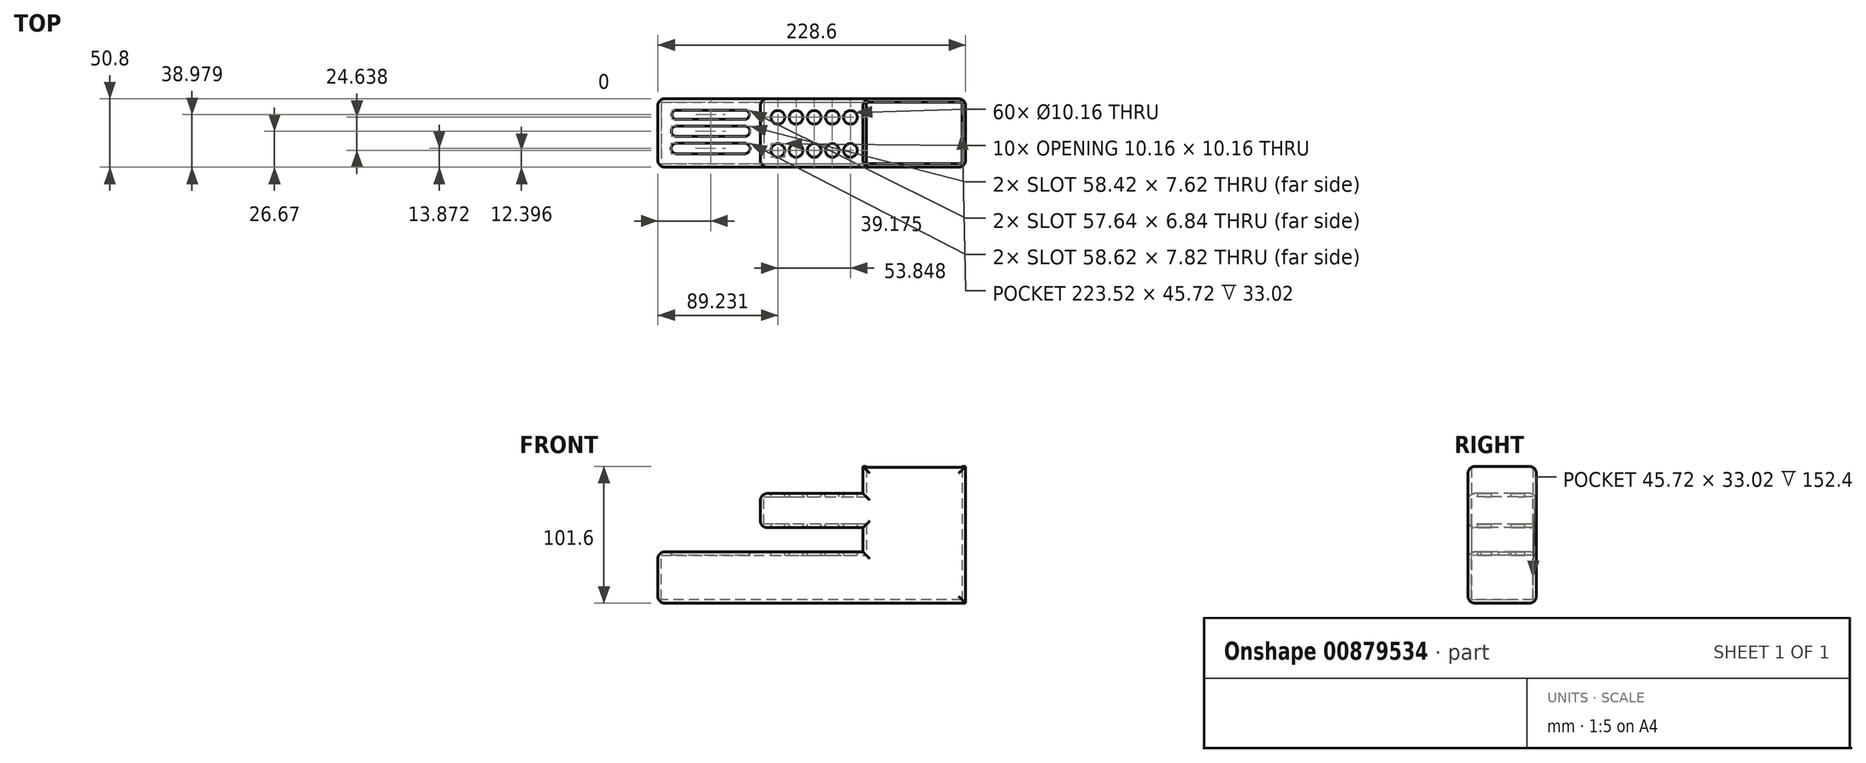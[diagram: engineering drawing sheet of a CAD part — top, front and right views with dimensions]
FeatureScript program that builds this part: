
annotation { "Feature Type Name" : "Feature", "Feature Type Description" : "" }
export const myFeature = defineFeature(function(context is Context, id is Id, definition is map)
    precondition{}
    {
        {
            var Q0;
            Q0=qCreatedBy(makeId("Front.planeOp"),FACE);
            var sketch = newSketch(context, id + "F0", { "sketchPlane" : qUnion([Q0])});
            skLineSegment(sketch, "E0", {"start": v(0, 45.54) * mm, "end": v(0, -56.06) * mm});
            skLineSegment(sketch, "E1", {"start": v(0, -56.06) * mm, "end": v(76.2, -56.06) * mm});
            skLineSegment(sketch, "E2", {"start": v(0, 45.54) * mm, "end": v(76.2, 45.54) * mm});
            skLineSegment(sketch, "E3", {"start": v(76.2, 45.54) * mm, "end": v(76.2, -56.06) * mm});
            skLineSegment(sketch, "E4", {"start": v(0, -56.06) * mm, "end": v(-152.4, -56.06) * mm});
            skLineSegment(sketch, "E5", {"start": v(-152.4, -56.06) * mm, "end": v(-152.4, -17.96) * mm});
            skLineSegment(sketch, "E6", {"start": v(-152.4, -17.96) * mm, "end": v(0, -17.96) * mm});
            skLineSegment(sketch, "E7", {"start": v(0, 0) * mm, "end": v(-76.2, 0) * mm});
            skLineSegment(sketch, "E8", {"start": v(-76.2, 0) * mm, "end": v(-76.2, 25.4) * mm});
            skLineSegment(sketch, "E9", {"start": v(-76.2, 25.4) * mm, "end": v(0, 25.4) * mm});
            skSolve(sketch);
        }
        {
            var Q0;
            Q0 = qSketchRegion(id + "F0", true);
            extrude(context, id + "F1", {"entities" : qUnion([Q0]), "oppositeDirection" : true, "depth" : 50.8 * mm, "offsetDistance" : 25.4 * mm});
        }
        {
            var Q0;
            Q0=makeQuery(id+"F1.opExtrude","SWEPT_FACE",FACE,{"disambiguationData":[OSD([sQuery(id+"F0.wireOp",EDGE,"E2")])]});
            shell(context, id + "F2", {"entities" : qUnion([Q0]), "thickness" : 2.54 * mm});
        }
        {
            var Q0;
            Q0=makeQuery(id+"F1.opExtrude","SWEPT_FACE",FACE,{"disambiguationData":[OSD([sQuery(id+"F0.wireOp",EDGE,"E9")])]});
            var sketch = newSketch(context, id + "F3", { "sketchPlane" : qUnion([Q0])});
            skCircle(sketch, "E10", {"center": v(-9.32, 12.4) * mm, "radius": 5.08 * mm});
            skCircle(sketch, "E11.0.1.0", {"center": v(-9.32, 37.03) * mm, "radius": 5.08 * mm});
            skCircle(sketch, "E11.1.0.0", {"center": v(-22.78, 12.4) * mm, "radius": 5.08 * mm});
            skCircle(sketch, "E11.1.1.0", {"center": v(-22.78, 37.03) * mm, "radius": 5.08 * mm});
            skCircle(sketch, "E11.2.0.0", {"center": v(-36.25, 12.4) * mm, "radius": 5.08 * mm});
            skCircle(sketch, "E11.2.1.0", {"center": v(-36.25, 37.03) * mm, "radius": 5.08 * mm});
            skCircle(sketch, "E11.3.0.0", {"center": v(-49.7, 12.4) * mm, "radius": 5.08 * mm});
            skCircle(sketch, "E11.3.1.0", {"center": v(-49.7, 37.03) * mm, "radius": 5.08 * mm});
            skCircle(sketch, "E11.4.0.0", {"center": v(-63.17, 12.4) * mm, "radius": 5.08 * mm});
            skCircle(sketch, "E11.4.1.0", {"center": v(-63.17, 37.03) * mm, "radius": 5.08 * mm});
            skLineSegment(sketch, "E11.direction1", {"start": v(-9.32, 12.4) * mm, "end": v(-22.78, 12.4) * mm, "construction": true});
            skLineSegment(sketch, "E11.direction2", {"start": v(-9.32, 12.4) * mm, "end": v(-9.32, 37.03) * mm, "construction": true});
            skSolve(sketch);
        }
        {
            var Q0;
            Q0 = qSketchRegion(id + "F3", true);
            extrude(context, id + "F4", {"entities" : qUnion([Q0]), "operationType" : NewBodyOperationType.REMOVE, "oppositeDirection" : true, "depth" : 76.2 * mm, "offsetDistance" : 25.4 * mm});
        }
        {
            var Q0;
            Q0=makeQuery(id+"F1.opExtrude","CAP_FACE",FACE,{"disambiguationData":[OSD([sQuery(id+"F0.wireOp",EDGE,"E0"),sQuery(id+"F0.wireOp",EDGE,"E1"),sQuery(id+"F0.wireOp",EDGE,"E2"),sQuery(id+"F0.wireOp",EDGE,"E3"),sQuery(id+"F0.wireOp",EDGE,"E4"),sQuery(id+"F0.wireOp",EDGE,"E5"),sQuery(id+"F0.wireOp",EDGE,"E6"),sQuery(id+"F0.wireOp",EDGE,"E7"),sQuery(id+"F0.wireOp",EDGE,"E8"),sQuery(id+"F0.wireOp",EDGE,"E9")])],"isStart":true});
            var Q1;
            Q1=makeQuery(id+"F1.opExtrude","CAP_FACE",FACE,{"disambiguationData":[OSD([sQuery(id+"F0.wireOp",EDGE,"E0"),sQuery(id+"F0.wireOp",EDGE,"E1"),sQuery(id+"F0.wireOp",EDGE,"E2"),sQuery(id+"F0.wireOp",EDGE,"E3"),sQuery(id+"F0.wireOp",EDGE,"E4"),sQuery(id+"F0.wireOp",EDGE,"E5"),sQuery(id+"F0.wireOp",EDGE,"E6"),sQuery(id+"F0.wireOp",EDGE,"E7"),sQuery(id+"F0.wireOp",EDGE,"E8"),sQuery(id+"F0.wireOp",EDGE,"E9")])],"isStart":false});
            var Q2;
            Q2=makeQuery(id+"F1.opExtrude","SWEPT_FACE",FACE,{"disambiguationData":[OSD([sQuery(id+"F0.wireOp",EDGE,"E5")])]});
            var Q3;
            Q3=makeQuery(id+"F1.opExtrude","SWEPT_FACE",FACE,{"disambiguationData":[OSD([sQuery(id+"F0.wireOp",EDGE,"E8")])]});
            fillet(context, id + "F5", {"entities" : qUnion([Q0, Q1, Q2, Q3]), "radius" : 5.08 * mm, "tangentPropagation" : true, "allowEdgeOverflow" : false});
        }
        {
            var Q0;
            Q0=makeQuery(id+"F1.opExtrude","SWEPT_FACE",FACE,{"disambiguationData":[OSD([sQuery(id+"F0.wireOp",EDGE,"E6")])]});
            var sketch = newSketch(context, id + "F6", { "sketchPlane" : qUnion([Q0])});
            skLineSegment(sketch, "E12", {"start": v(-138.63, 9.96) * mm, "end": v(-87.83, 9.96) * mm});
            skLineSegment(sketch, "E13", {"start": v(-138.63, 17.78) * mm, "end": v(-87.83, 17.78) * mm});
            skArc(sketch, "E14", {"start": v(-138.63, 9.96) * mm, "mid": v(-142.53, 13.87) * mm, "end": v(-138.63, 17.78) * mm});
            skArc(sketch, "E15", {"start": v(-87.83, 9.96) * mm, "mid": v(-83.92, 13.87) * mm, "end": v(-87.83, 17.78) * mm});
            skLineSegment(sketch, "E16", {"start": v(-138.63, 22.86) * mm, "end": v(-87.83, 22.86) * mm});
            skLineSegment(sketch, "E17", {"start": v(-138.63, 30.48) * mm, "end": v(-87.83, 30.48) * mm});
            skArc(sketch, "E18", {"start": v(-138.63, 22.86) * mm, "mid": v(-142.44, 26.67) * mm, "end": v(-138.63, 30.48) * mm});
            skArc(sketch, "E19", {"start": v(-87.83, 30.48) * mm, "mid": v(-84.02, 26.67) * mm, "end": v(-87.83, 22.86) * mm});
            skLineSegment(sketch, "E20", {"start": v(-138.63, 35.56) * mm, "end": v(-87.83, 35.56) * mm});
            skLineSegment(sketch, "E21", {"start": v(-138.63, 42.4) * mm, "end": v(-87.83, 42.4) * mm});
            skArc(sketch, "E22", {"start": v(-138.63, 35.56) * mm, "mid": v(-142.04, 38.98) * mm, "end": v(-138.63, 42.4) * mm});
            skArc(sketch, "E23", {"start": v(-87.83, 35.56) * mm, "mid": v(-84.4, 38.98) * mm, "end": v(-87.83, 42.4) * mm});
            skSolve(sketch);
        }
        {
            var Q0;
            Q0 = qSketchRegion(id + "F6", true);
            extrude(context, id + "F7", {"entities" : qUnion([Q0]), "operationType" : NewBodyOperationType.REMOVE, "oppositeDirection" : true, "depth" : 25.4 * mm, "offsetDistance" : 25.4 * mm});
        }
    });
